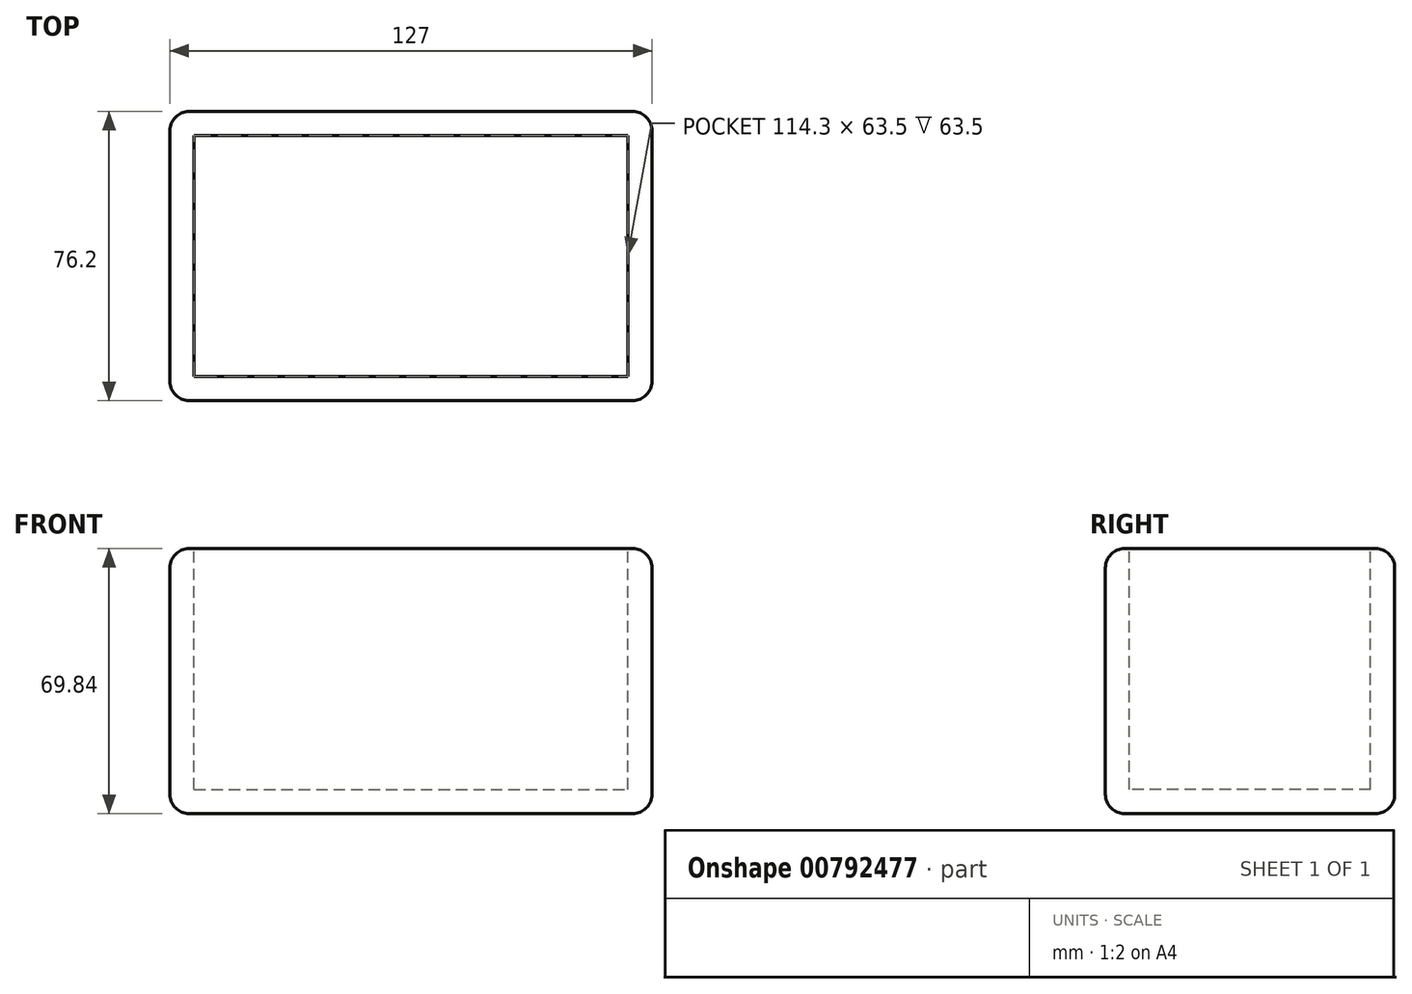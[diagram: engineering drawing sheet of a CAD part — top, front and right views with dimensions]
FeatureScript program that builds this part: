
annotation { "Feature Type Name" : "Feature", "Feature Type Description" : "" }
export const myFeature = defineFeature(function(context is Context, id is Id, definition is map)
    precondition{}
    {
        {
            var Q0;
            Q0=qCreatedBy(makeId("Front.planeOp"),FACE);
            var sketch = newSketch(context, id + "F0", { "sketchPlane" : qUnion([Q0])});
            skLineSegment(sketch, "E0.bottom", {"start": v(-63.5, 34.92) * mm, "end": v(63.5, 34.92) * mm});
            skLineSegment(sketch, "E0.top", {"start": v(-63.5, -34.93) * mm, "end": v(63.5, -34.93) * mm});
            skLineSegment(sketch, "E0.left", {"start": v(-63.5, 34.92) * mm, "end": v(-63.5, -34.93) * mm});
            skLineSegment(sketch, "E0.right", {"start": v(63.5, 34.92) * mm, "end": v(63.5, -34.93) * mm});
            skPoint(sketch, "E0.middle", {"position": v(0, 0) * mm});
            skSolve(sketch);
        }
        {
            var Q0;
            Q0=makeQuery(id+"F0.imprint","IMPRINT",FACE,{"disambiguationData":[TD([[makeQuery(id+"F0.imprint","IMPRINT",EDGE,{"derivedFrom":sQuery(id+"F0.wireOp",EDGE,"E0.bottom")}),-1.0]])]});
            extrude(context, id + "F1", {"entities" : qUnion([Q0]), "endBound" : BoundingType.SYMMETRIC, "depth" : 76.2 * mm, "offsetDistance" : 25.4 * mm});
        }
        {
            var Q0;
            Q0=makeQuery(id+"F1.opExtrude","SWEPT_FACE",FACE,{"disambiguationData":[OSD([sQuery(id+"F0.wireOp",EDGE,"E0.bottom")])]});
            var sketch = newSketch(context, id + "F2", { "sketchPlane" : qUnion([Q0])});
            skLineSegment(sketch, "E1.bottom", {"start": v(-57.15, 31.75) * mm, "end": v(57.15, 31.75) * mm});
            skLineSegment(sketch, "E1.top", {"start": v(-57.15, -31.75) * mm, "end": v(57.15, -31.75) * mm});
            skLineSegment(sketch, "E1.left", {"start": v(-57.15, 31.75) * mm, "end": v(-57.15, -31.75) * mm});
            skLineSegment(sketch, "E1.right", {"start": v(57.15, 31.75) * mm, "end": v(57.15, -31.75) * mm});
            skPoint(sketch, "E1.middle", {"position": v(0, 0) * mm});
            skSolve(sketch);
        }
        {
            var Q0;
            Q0=makeQuery(id+"F2.imprint","IMPRINT",FACE,{"disambiguationData":[TD([[makeQuery(id+"F2.imprint","IMPRINT",EDGE,{"derivedFrom":sQuery(id+"F2.wireOp",EDGE,"E1.bottom")}),-1.0]])]});
            extrude(context, id + "F3", {"entities" : qUnion([Q0]), "operationType" : NewBodyOperationType.REMOVE, "oppositeDirection" : true, "depth" : 63.5 * mm, "offsetDistance" : 25.4 * mm});
        }
        {
            var Q0;
            Q0=makeQuery(id+"F1.opExtrude","CAP_EDGE",EDGE,{"disambiguationData":[OSD([sQuery(id+"F0.wireOp",EDGE,"E0.bottom")])],"isStart":false});
            var Q1;
            Q1=makeQuery(id+"F1.opExtrude","SWEPT_EDGE",EDGE,{"disambiguationData":[OSD([sQuery(id+"F0.wireOp",EDGE,"E0.bottom"),sQuery(id+"F0.wireOp",EDGE,"E0.left")])]});
            var Q2;
            Q2=makeQuery(id+"F1.opExtrude","CAP_EDGE",EDGE,{"disambiguationData":[OSD([sQuery(id+"F0.wireOp",EDGE,"E0.bottom")])],"isStart":true});
            var Q3;
            Q3=makeQuery(id+"F1.opExtrude","SWEPT_EDGE",EDGE,{"disambiguationData":[OSD([sQuery(id+"F0.wireOp",EDGE,"E0.bottom"),sQuery(id+"F0.wireOp",EDGE,"E0.right")])]});
            var Q4;
            Q4=makeQuery(id+"F1.opExtrude","CAP_EDGE",EDGE,{"disambiguationData":[OSD([sQuery(id+"F0.wireOp",EDGE,"E0.right")])],"isStart":true});
            var Q5;
            Q5=makeQuery(id+"F1.opExtrude","CAP_EDGE",EDGE,{"disambiguationData":[OSD([sQuery(id+"F0.wireOp",EDGE,"E0.left")])],"isStart":true});
            var Q6;
            Q6=makeQuery(id+"F1.opExtrude","CAP_EDGE",EDGE,{"disambiguationData":[OSD([sQuery(id+"F0.wireOp",EDGE,"E0.top")])],"isStart":true});
            var Q7;
            Q7=makeQuery(id+"F1.opExtrude","SWEPT_EDGE",EDGE,{"disambiguationData":[OSD([sQuery(id+"F0.wireOp",EDGE,"E0.top"),sQuery(id+"F0.wireOp",EDGE,"E0.left")])]});
            var Q8;
            Q8=makeQuery(id+"F1.opExtrude","CAP_EDGE",EDGE,{"disambiguationData":[OSD([sQuery(id+"F0.wireOp",EDGE,"E0.top")])],"isStart":false});
            var Q9;
            Q9=makeQuery(id+"F1.opExtrude","CAP_EDGE",EDGE,{"disambiguationData":[OSD([sQuery(id+"F0.wireOp",EDGE,"E0.right")])],"isStart":false});
            var Q10;
            Q10=makeQuery(id+"F1.opExtrude","SWEPT_EDGE",EDGE,{"disambiguationData":[OSD([sQuery(id+"F0.wireOp",EDGE,"E0.top"),sQuery(id+"F0.wireOp",EDGE,"E0.right")])]});
            var Q11;
            Q11=makeQuery(id+"F1.opExtrude","CAP_EDGE",EDGE,{"disambiguationData":[OSD([sQuery(id+"F0.wireOp",EDGE,"E0.left")])],"isStart":false});
            fillet(context, id + "F4", {"entities" : qUnion([Q0, Q1, Q2, Q3, Q4, Q5, Q6, Q7, Q8, Q9, Q10, Q11]), "radius" : 5.08 * mm, "tangentPropagation" : true, "allowEdgeOverflow" : false});
        }
    });
